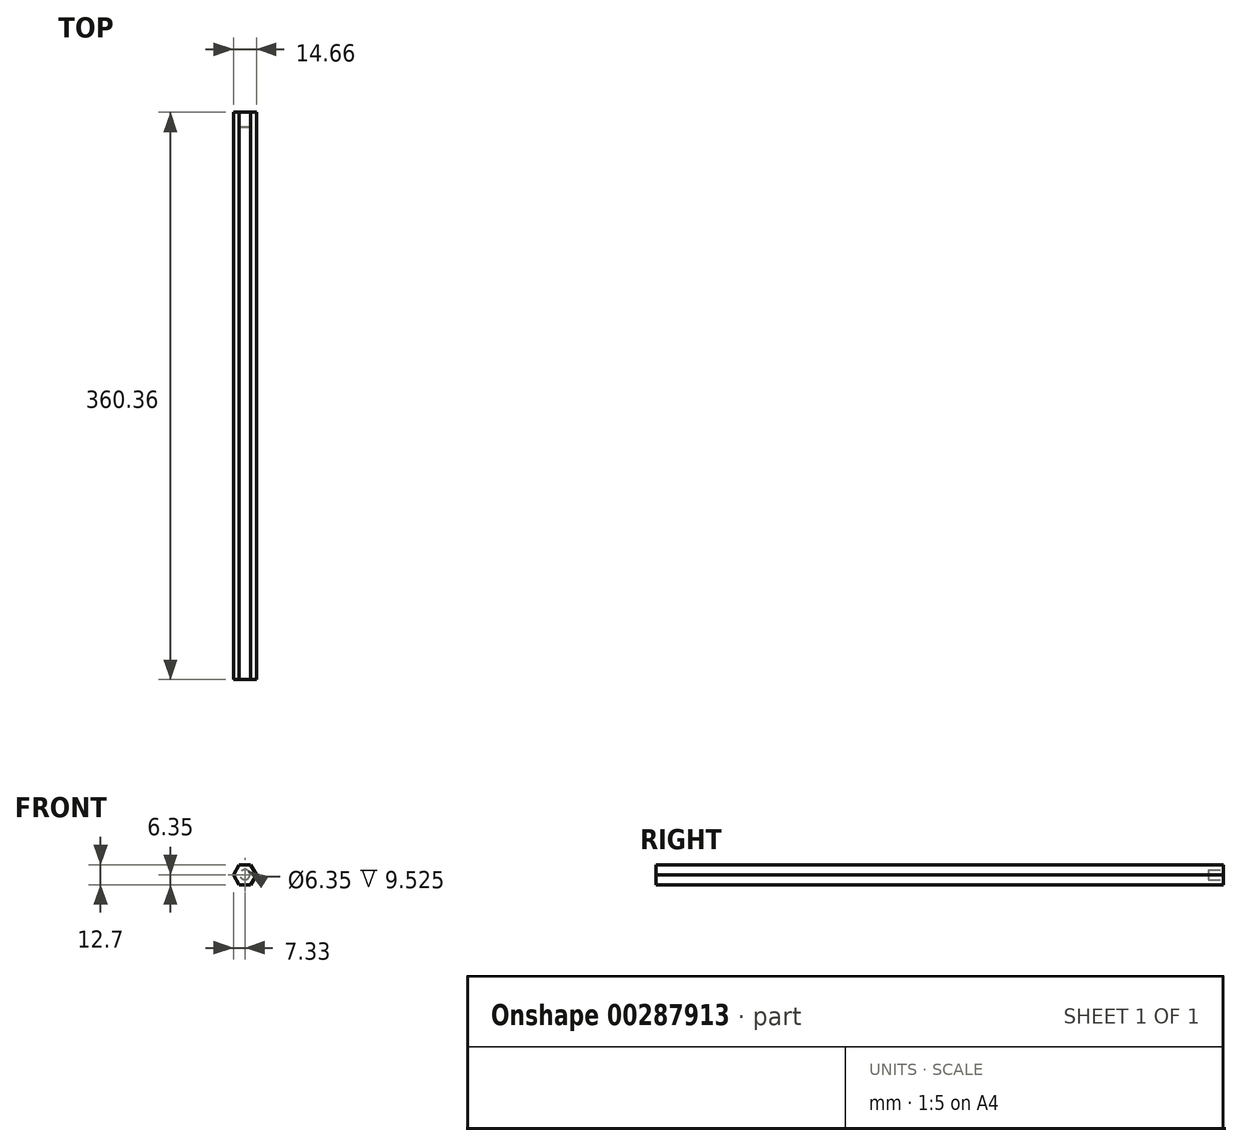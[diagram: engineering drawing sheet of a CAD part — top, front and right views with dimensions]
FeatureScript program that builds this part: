
annotation { "Feature Type Name" : "Feature", "Feature Type Description" : "" }
export const myFeature = defineFeature(function(context is Context, id is Id, definition is map)
    precondition{}
    {
        {
            var Q0;
            Q0=qCreatedBy(makeId("Front.planeOp"),FACE);
            var sketch = newSketch(context, id + "F0", { "sketchPlane" : qUnion([Q0])});
            skCircle(sketch, "E0.cCircle", {"center": v(0, 0) * mm, "radius": 6.35 * mm, "construction": true});
            skLineSegment(sketch, "E0.0", {"start": v(-3.67, 6.35) * mm, "end": v(3.67, 6.35) * mm});
            skLineSegment(sketch, "E0.1", {"start": v(3.67, 6.35) * mm, "end": v(7.33, 0) * mm});
            skLineSegment(sketch, "E0.2", {"start": v(7.33, 0) * mm, "end": v(3.67, -6.35) * mm});
            skLineSegment(sketch, "E0.3", {"start": v(3.67, -6.35) * mm, "end": v(-3.67, -6.35) * mm});
            skLineSegment(sketch, "E0.4", {"start": v(-3.67, -6.35) * mm, "end": v(-7.33, 0) * mm});
            skLineSegment(sketch, "E0.5", {"start": v(-7.33, 0) * mm, "end": v(-3.67, 6.35) * mm});
            skPoint(sketch, "E0.0.midPoint", {"position": v(0, 6.35) * mm});
            skSolve(sketch);
        }
        {
            var Q0;
            Q0 = qSketchRegion(id + "F0", true);
            extrude(context, id + "F1", {"entities" : qUnion([Q0]), "depth" : 360.36 * mm});
        }
        {
            var Q0;
            Q0=makeQuery(id+"F1.opExtrude","CAP_FACE",FACE,{"disambiguationData":[OSD([sQuery(id+"F0.wireOp",EDGE,"E0.0"),sQuery(id+"F0.wireOp",EDGE,"E0.1"),sQuery(id+"F0.wireOp",EDGE,"E0.2"),sQuery(id+"F0.wireOp",EDGE,"E0.3"),sQuery(id+"F0.wireOp",EDGE,"E0.4"),sQuery(id+"F0.wireOp",EDGE,"E0.5")])],"isStart":true});
            var sketch = newSketch(context, id + "F2", { "sketchPlane" : qUnion([Q0])});
            skCircle(sketch, "E1", {"center": v(0, 0) * mm, "radius": 3.17 * mm});
            skSolve(sketch);
        }
        {
            var Q0;
            Q0 = qSketchRegion(id + "F2", true);
            extrude(context, id + "F3", {"entities" : qUnion([Q0]), "operationType" : NewBodyOperationType.REMOVE, "oppositeDirection" : true, "depth" : 9.52 * mm});
        }
    });
